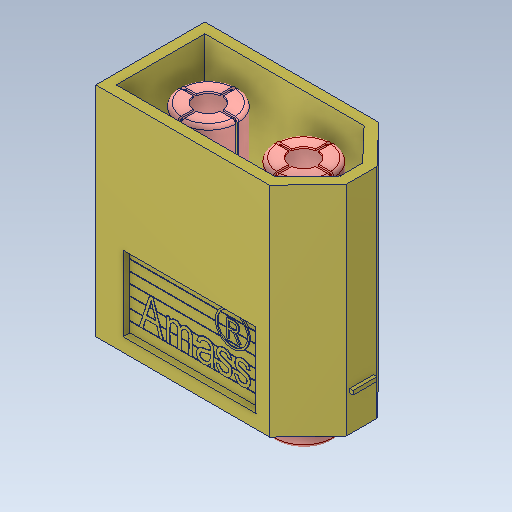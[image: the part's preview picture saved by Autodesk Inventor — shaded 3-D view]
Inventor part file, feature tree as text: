
AUTODESK INVENTOR PART (.ipt)
format: ipt  version: 2020 (Build 240168000, 168)  size: 925,696 bytes
history: mixed  units: in
note: dims shown in document units (in); Inventor stores cm internally (conversion verified against a paired STEP export)
features: fillet x2, imported_body x1
ambient origin geometry x8: Origin, YZ Plane, XZ Plane, XY Plane, X Axis, Y Axis, Z Axis, Center Point
bodies: Solid1 (imported_parasolid), Solid2 (imported_parasolid)
feature tree (3):
  fillet  "Fillet6"  [1 undecoded]
  fillet  "Fillet7"  [1 undecoded]
  imported_body  NMx_Import_Brep_tag  [imported B-rep: ~18 faces, bbox_mm=[10.741657, 0.0, 1.745829]]
note: 2 required parameter values undecoded (feature->parameter linkage not recoverable at this tier; creation-order binding heuristic only, values carry confidence <= 0.55)
